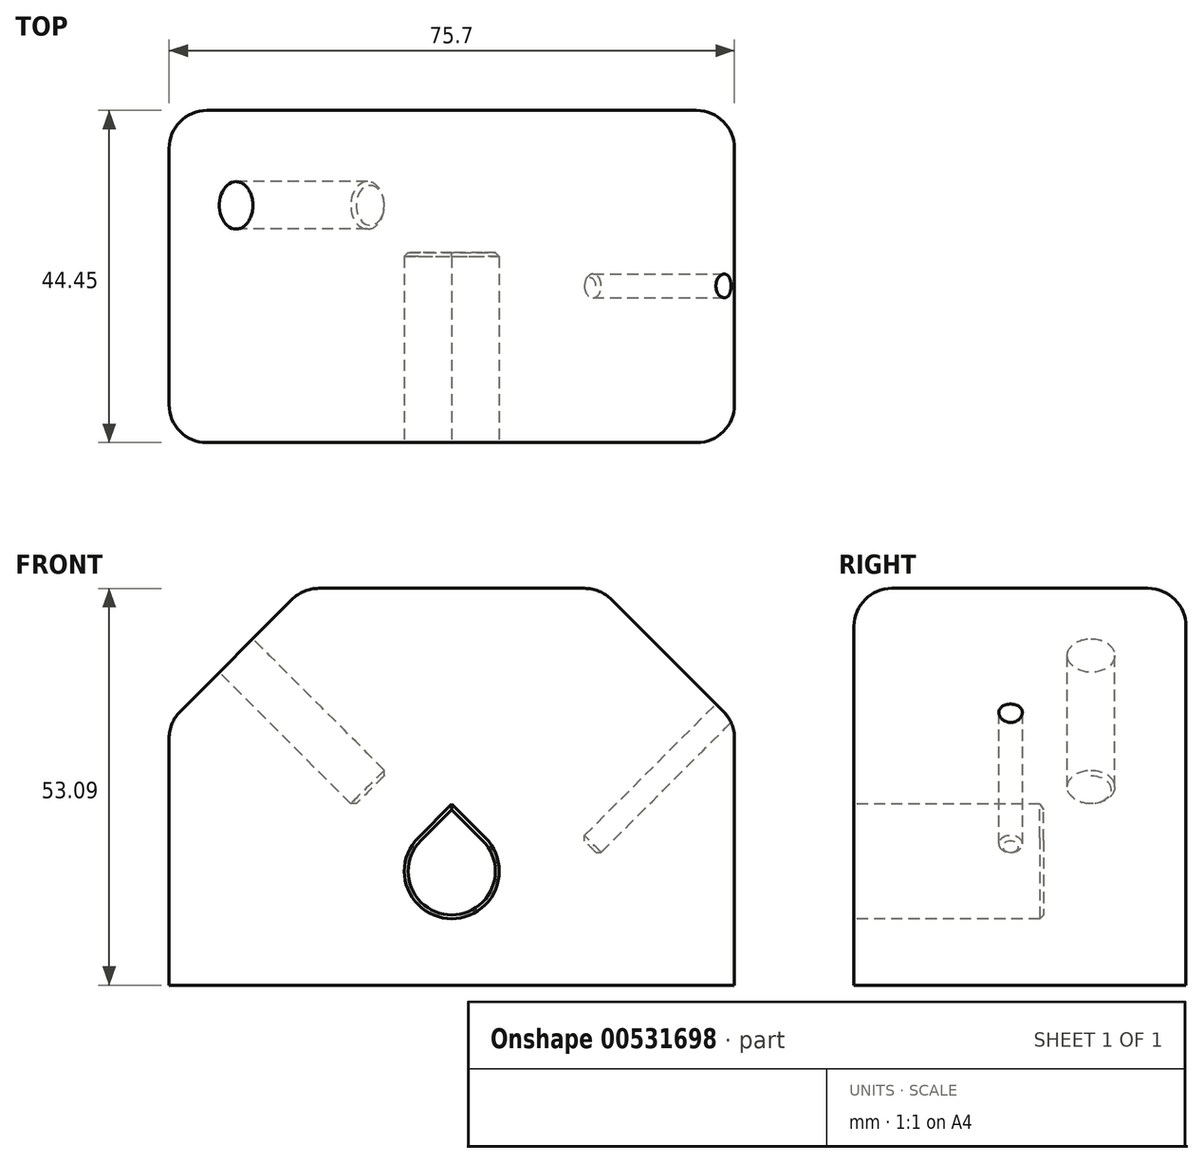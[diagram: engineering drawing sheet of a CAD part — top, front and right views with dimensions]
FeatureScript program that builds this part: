
annotation { "Feature Type Name" : "Feature", "Feature Type Description" : "" }
export const myFeature = defineFeature(function(context is Context, id is Id, definition is map)
    precondition{}
    {
        {
            var Q0;
            Q0=qCreatedBy(makeId("Front.planeOp"),FACE);
            var sketch = newSketch(context, id + "F0", { "sketchPlane" : qUnion([Q0])});
            skLineSegment(sketch, "E0", {"start": v(0, 0) * mm, "end": v(-37.85, 0) * mm});
            skLineSegment(sketch, "E1", {"start": v(-37.85, 0) * mm, "end": v(-37.85, 35.13) * mm});
            skLineSegment(sketch, "E2", {"start": v(-37.85, 35.13) * mm, "end": v(-19.9, 53.1) * mm});
            skLineSegment(sketch, "E3", {"start": v(-19.9, 53.1) * mm, "end": v(0, 53.1) * mm});
            skLineSegment(sketch, "E4", {"start": v(0, 53.1) * mm, "end": v(0, 0) * mm, "construction": true});
            skPoint(sketch, "E5", {"position": v(-28.87, 44.11) * mm});
            skPoint(sketch, "E6", {"position": v(-24.38, 48.6) * mm});
            skPoint(sketch, "E7", {"position": v(-33.36, 39.62) * mm});
            skLineSegment(sketch, "E8.MirrorCS", {"start": v(19.9, 53.1) * mm, "end": v(0, 53.1) * mm});
            skLineSegment(sketch, "E9.MirrorCS", {"start": v(37.85, 35.13) * mm, "end": v(19.9, 53.1) * mm});
            skPoint(sketch, "E10.MirrorP", {"position": v(28.87, 44.11) * mm});
            skLineSegment(sketch, "E11.MirrorCS", {"start": v(37.85, 0) * mm, "end": v(37.85, 35.13) * mm});
            skLineSegment(sketch, "E12.MirrorCS", {"start": v(0, 0) * mm, "end": v(37.85, 0) * mm});
            skLineSegment(sketch, "E13", {"start": v(-28.87, 44.11) * mm, "end": v(0, 15.24) * mm, "construction": true});
            skLineSegment(sketch, "E14", {"start": v(0, 15.24) * mm, "end": v(28.87, 44.11) * mm, "construction": true});
            skSolve(sketch);
        }
        {
            var Q0;
            Q0=qSketchRegion(id+"F0",true);
            extrude(context, id + "F1", {"entities" : qUnion([Q0]), "depth" : 31.75 * mm, "offsetDistance" : 25.4 * mm, "hasSecondDirection" : true, "secondDirectionOppositeDirection" : true, "secondDirectionDepth" : 12.7 * mm});
        }
        {
            var Q0;
            Q0=makeQuery(id+"F1.opExtrude","SWEPT_FACE",FACE,{"disambiguationData":[OSD([sQuery(id+"F0.wireOp",EDGE,"E2")])]});
            var sketch = newSketch(context, id + "F2", { "sketchPlane" : qUnion([Q0])});
            skPoint(sketch, "E15.0", {"position": v(0, 10.78) * mm});
            skCircle(sketch, "E16", {"center": v(0, 10.78) * mm, "radius": 3.18 * mm});
            skSolve(sketch);
        }
        {
            var Q0;
            Q0=qSketchRegion(id+"F2",true);
            extrude(context, id + "F3", {"entities" : qUnion([Q0]), "operationType" : NewBodyOperationType.REMOVE, "oppositeDirection" : true, "depth" : 25.4 * mm, "offsetDistance" : 25.4 * mm});
        }
        {
            var Q0;
            Q0=makeQuery(id+"F1.opExtrude","SWEPT_FACE",FACE,{"disambiguationData":[OSD([sQuery(id+"F0.wireOp",EDGE,"E9.MirrorCS")])]});
            var sketch = newSketch(context, id + "F4", { "sketchPlane" : qUnion([Q0])});
            skPoint(sketch, "E17.0", {"position": v(-10.78, 0) * mm});
            skCircle(sketch, "E18", {"center": v(-10.78, 0) * mm, "radius": 1.59 * mm});
            skSolve(sketch);
        }
        {
            var Q0;
            Q0=qSketchRegion(id+"F4",true);
            extrude(context, id + "F5", {"entities" : qUnion([Q0]), "operationType" : NewBodyOperationType.REMOVE, "oppositeDirection" : true, "depth" : 25.4 * mm, "offsetDistance" : 25.4 * mm});
        }
        {
            var Q0;
            Q0=makeQuery(id+"F1.opExtrude","CAP_FACE",FACE,{"disambiguationData":[OSD([sQuery(id+"F0.wireOp",EDGE,"E0"),sQuery(id+"F0.wireOp",EDGE,"E1"),sQuery(id+"F0.wireOp",EDGE,"E2"),sQuery(id+"F0.wireOp",EDGE,"E3"),sQuery(id+"F0.wireOp",EDGE,"E8.MirrorCS"),sQuery(id+"F0.wireOp",EDGE,"E9.MirrorCS"),sQuery(id+"F0.wireOp",EDGE,"E11.MirrorCS"),sQuery(id+"F0.wireOp",EDGE,"E12.MirrorCS")])],"isStart":false});
            var sketch = newSketch(context, id + "F6", { "sketchPlane" : qUnion([Q0])});
            skPoint(sketch, "E19.0", {"position": v(0, 15.24) * mm});
            skArc(sketch, "E20", {"start": v(-4.5, 19.73) * mm, "mid": v(0, 8.9) * mm, "end": v(4.5, 19.73) * mm});
            skLineSegment(sketch, "E21.0", {"start": v(-28.87, 44.11) * mm, "end": v(0, 15.24) * mm, "construction": true});
            skLineSegment(sketch, "E21.1", {"start": v(0, 15.24) * mm, "end": v(28.87, 44.11) * mm, "construction": true});
            skLineSegment(sketch, "E22", {"start": v(-4.5, 19.73) * mm, "end": v(0, 24.22) * mm});
            skLineSegment(sketch, "E23", {"start": v(0, 24.22) * mm, "end": v(4.5, 19.73) * mm});
            skSolve(sketch);
        }
        {
            var Q0;
            Q0=qSketchRegion(id+"F6",true);
            extrude(context, id + "F7", {"entities" : qUnion([Q0]), "operationType" : NewBodyOperationType.REMOVE, "oppositeDirection" : true, "depth" : 25.4 * mm, "offsetDistance" : 25.4 * mm});
        }
        {
            var Q0;
            Q0=makeQuery(id+"F1.opExtrude","CAP_EDGE",EDGE,{"disambiguationData":[OSD([sQuery(id+"F0.wireOp",EDGE,"E1")])],"isStart":true});
            var Q1;
            Q1=makeQuery(id+"F1.opExtrude","CAP_EDGE",EDGE,{"disambiguationData":[OSD([sQuery(id+"F0.wireOp",EDGE,"E2")])],"isStart":true});
            var Q2;
            Q2=makeQuery(id+"F1.opExtrude","CAP_EDGE",EDGE,{"disambiguationData":[OSD([sQuery(id+"F0.wireOp",EDGE,"E3"),sQuery(id+"F0.wireOp",EDGE,"E8.MirrorCS")])],"isStart":true});
            var Q3;
            Q3=makeQuery(id+"F1.opExtrude","CAP_EDGE",EDGE,{"disambiguationData":[OSD([sQuery(id+"F0.wireOp",EDGE,"E9.MirrorCS")])],"isStart":true});
            var Q4;
            Q4=makeQuery(id+"F1.opExtrude","CAP_EDGE",EDGE,{"disambiguationData":[OSD([sQuery(id+"F0.wireOp",EDGE,"E11.MirrorCS")])],"isStart":true});
            var Q5;
            Q5=makeQuery(id+"F1.opExtrude","SWEPT_EDGE",EDGE,{"disambiguationData":[OSD([sQuery(id+"F0.wireOp",EDGE,"E2"),sQuery(id+"F0.wireOp",EDGE,"E3")])]});
            var Q6;
            Q6=makeQuery(id+"F1.opExtrude","SWEPT_EDGE",EDGE,{"disambiguationData":[OSD([sQuery(id+"F0.wireOp",EDGE,"E1"),sQuery(id+"F0.wireOp",EDGE,"E2")])]});
            var Q7;
            Q7=makeQuery(id+"F1.opExtrude","CAP_EDGE",EDGE,{"disambiguationData":[OSD([sQuery(id+"F0.wireOp",EDGE,"E2")])],"isStart":false});
            var Q8;
            Q8=makeQuery(id+"F1.opExtrude","CAP_EDGE",EDGE,{"disambiguationData":[OSD([sQuery(id+"F0.wireOp",EDGE,"E1")])],"isStart":false});
            var Q9;
            Q9=makeQuery(id+"F1.opExtrude","CAP_EDGE",EDGE,{"disambiguationData":[OSD([sQuery(id+"F0.wireOp",EDGE,"E3"),sQuery(id+"F0.wireOp",EDGE,"E8.MirrorCS")])],"isStart":false});
            var Q10;
            Q10=makeQuery(id+"F1.opExtrude","SWEPT_EDGE",EDGE,{"disambiguationData":[OSD([sQuery(id+"F0.wireOp",EDGE,"E8.MirrorCS"),sQuery(id+"F0.wireOp",EDGE,"E9.MirrorCS")])]});
            var Q11;
            Q11=makeQuery(id+"F1.opExtrude","CAP_EDGE",EDGE,{"disambiguationData":[OSD([sQuery(id+"F0.wireOp",EDGE,"E9.MirrorCS")])],"isStart":false});
            var Q12;
            Q12=makeQuery(id+"F1.opExtrude","CAP_EDGE",EDGE,{"disambiguationData":[OSD([sQuery(id+"F0.wireOp",EDGE,"E11.MirrorCS")])],"isStart":false});
            var Q13;
            Q13=makeQuery(id+"F1.opExtrude","SWEPT_EDGE",EDGE,{"disambiguationData":[OSD([sQuery(id+"F0.wireOp",EDGE,"E9.MirrorCS"),sQuery(id+"F0.wireOp",EDGE,"E11.MirrorCS")])]});
            fillet(context, id + "F8", {"entities" : qUnion([Q0, Q1, Q2, Q3, Q4, Q5, Q6, Q7, Q8, Q9, Q10, Q11, Q12, Q13]), "radius" : 5.08 * mm, "tangentPropagation" : true, "allowEdgeOverflow" : false});
        }
        {
            var Q0;
            Q0=makeQuery(id+"F7.boolean.opBoolean","COPY",EDGE,{"derivedFrom":makeQuery(id+"F7.opExtrude","CAP_EDGE",EDGE,{"disambiguationData":[OSD([sQuery(id+"F6.wireOp",EDGE,"E20")])],"isStart":false})});
            var Q1;
            Q1=makeQuery(id+"F3.boolean.opBoolean","COPY",EDGE,{"derivedFrom":makeQuery(id+"F3.opExtrude","CAP_EDGE",EDGE,{"disambiguationData":[OSD([sQuery(id+"F2.wireOp",EDGE,"E16")])],"isStart":false})});
            var Q2;
            Q2=makeQuery(id+"F5.boolean.opBoolean","COPY",EDGE,{"derivedFrom":makeQuery(id+"F5.opExtrude","CAP_EDGE",EDGE,{"disambiguationData":[OSD([sQuery(id+"F4.wireOp",EDGE,"E18")])],"isStart":false})});
            chamfer(context, id + "F9", {"entities" : qUnion([Q0, Q1, Q2]), "width" : 0.5 * mm, "tangentPropagation" : true});
        }
    });
